# Revit family: Mailboxes_4C-Salsbury_Industries-Front_Load-3_Door_High_Units
name_source: partatom
category: Specialty Equipment
revit_build: Autodesk Revit 2016 (Build: 20150714_1515(x64)
units: mm (PartAtom-declared; Revit-internal decimal feet)

## family parameters
Always vertical = Yes
Cut with Voids When Loaded = No
Host = Wall
OmniClass Number = 23.40.90.14.11
OmniClass Title = Mail Boxes
Part Type = Normal
Room Calculation Point = No
Round Connector Dimension = Use Diameter
Shared = No

## types (4) — shared parameters
Assembly Code = C1030910
Assembly Description = Mailboxes
Back Enclosure Material = Aluminum - Salsbury Finish - Anodized
Bottom Back Plate = Yes
Depth = 17.025"
Door Slot R2 = 3700 Series 4C Door Configurations : Empty
Height = 13.000"
Left Inside Wall = Yes
Lock Material = Stainless Steel - Salsbury Finish -  Polished
Manufacturer = Salsbury Industries
MasterFormat Number = 10 55 00
MasterFormat Title = Postal Specialties
OmniClass 23 Number = 23.40.90.14.11
OmniClass 23 Title = Mail Boxes
Right Inside Wall = Yes
Top Back Plate = Yes
Type Comments = 4C Standard Horizontal Mailbox - Front Loading
URL = www.mailboxes.com
Version = 3.0 (06/30/17)
Vertical Center Divider = Yes

## per-type parameters (varying)
| type | Description | Door Slot L1 | Door Slot L2 | Door Slot L3 | Door Slot R1 | Door Slot R3 | Width |
| 3703D-04 FL | 3 Door High Unit:  4 MB1, OM2 | 3700 Series 4C Door Configurations : MB1 Door | 3700 Series 4C Door Configurations : MB1 Door w/ Divider | 3700 Series 4C Door Configurations : MB1 Door w/ Divider | 3700 Series 4C Door Configurations : MB1 Door | 3700 Series 4C OM2 Configuration : OM2-FL | 31.098" |
| 3703S-01 FL | 3 Door High Unit:  1 MB1, OM2 | 3700 Series 4C Door Configurations : Empty | 3700 Series 4C Door Configurations : Empty | 3700 Series 4C Door Configurations : Empty | 3700 Series 4C Door Configurations : MB1 Door | 3700 Series 4C OM2 Configuration : OM2-FL | 16.344" |
| 3703D-2P FL | 3 Door High Unit:  2 PL3 | 3700 Series 4C Door Configurations : Empty | 3700 Series 4C Door Configurations : Empty | 3700 Series 4C Parcel Configurations : PL3 | 3700 Series 4C Door Configurations : Empty | 3700 Series 4C Parcel Configurations : PL3 | 31.098" |
| 3703S-1P FL | 3 Door High Unit:  1 PL3 | 3700 Series 4C Door Configurations : Empty | 3700 Series 4C Door Configurations : Empty | 3700 Series 4C Door Configurations : Empty | 3700 Series 4C Door Configurations : Empty | 3700 Series 4C Parcel Configurations : PL3 | 16.344" |

note: column(s) folded — value = type name in every type: Model

## geometry (parser evidence)
native form markers: Blend x2, Extrusion x1, Sweep x12
no freeform markers — native parametric forms only
